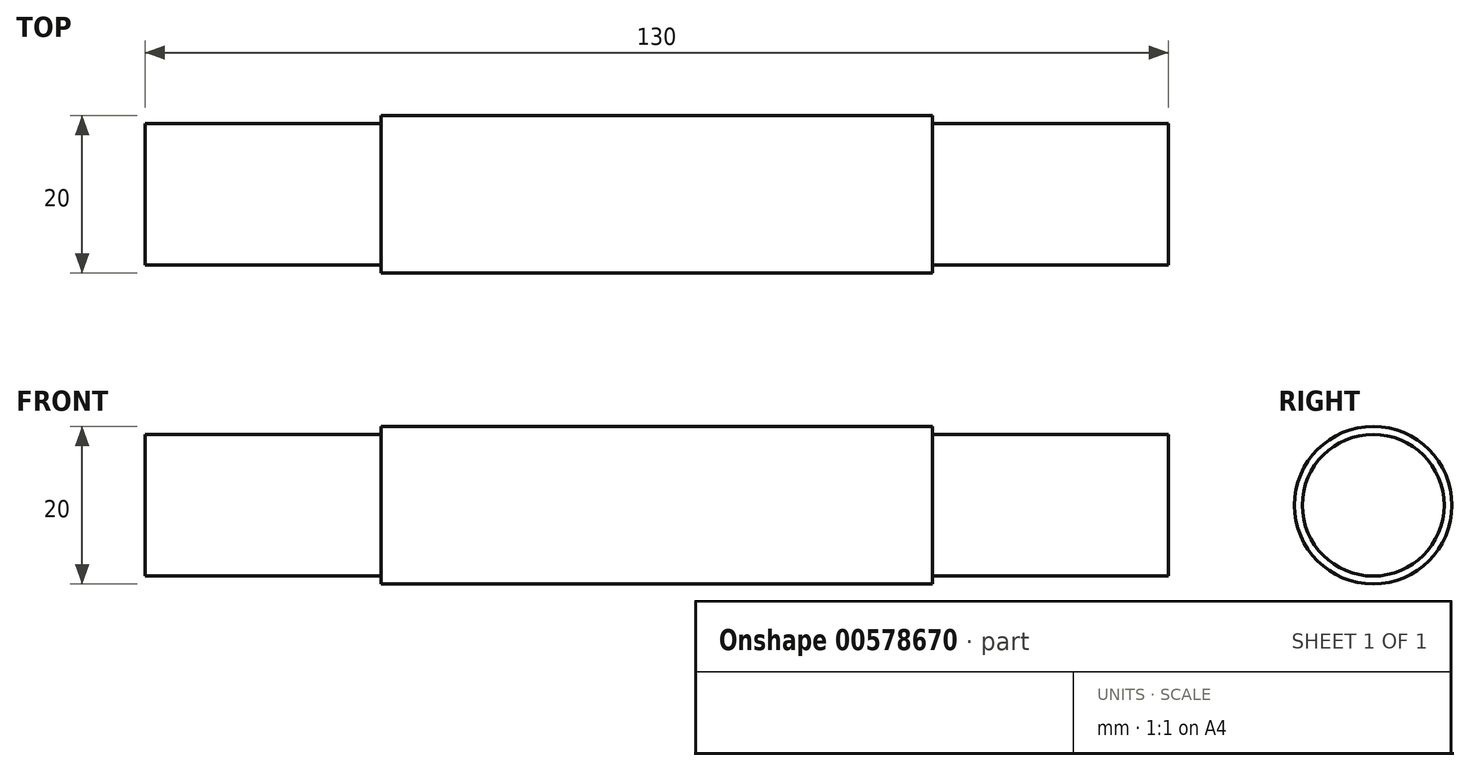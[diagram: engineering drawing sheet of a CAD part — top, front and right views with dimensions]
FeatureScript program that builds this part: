
annotation { "Feature Type Name" : "Feature", "Feature Type Description" : "" }
export const myFeature = defineFeature(function(context is Context, id is Id, definition is map)
    precondition{}
    {
        {
            var Q0;
            Q0=qCreatedBy(makeId("Top.planeOp"),FACE);
            var sketch = newSketch(context, id + "F0", { "sketchPlane" : qUnion([Q0])});
            skLineSegment(sketch, "E0", {"start": v(-42.44, 9) * mm, "end": v(-12.44, 9) * mm});
            skLineSegment(sketch, "E1", {"start": v(-12.44, 9) * mm, "end": v(-12.44, 10) * mm});
            skLineSegment(sketch, "E2", {"start": v(-12.44, 10) * mm, "end": v(57.56, 10) * mm});
            skLineSegment(sketch, "E3", {"start": v(57.56, 10) * mm, "end": v(57.56, 9) * mm});
            skLineSegment(sketch, "E4", {"start": v(57.56, 9) * mm, "end": v(87.56, 9) * mm});
            skLineSegment(sketch, "E5", {"start": v(87.56, 9) * mm, "end": v(87.56, 0) * mm});
            skLineSegment(sketch, "E6", {"start": v(-42.44, 9) * mm, "end": v(-42.44, 0) * mm});
            skLineSegment(sketch, "E7", {"start": v(-53.5, 0) * mm, "end": v(73.3, 0) * mm, "construction": true});
            skLineSegment(sketch, "E8", {"start": v(-42.44, 0) * mm, "end": v(87.56, 0) * mm});
            skLineSegment(sketch, "E9", {"start": v(22.56, 54.38) * mm, "end": v(22.56, -21.7) * mm, "construction": true});
            skSolve(sketch);
        }
        {
            var Q0;
            Q0=qSketchRegion(id+"F0",true);
            var Q1;
            Q1=sQuery(id+"F0.wireOp",EDGE,"E7");
            revolve(context, id + "F1", {"entities" : qUnion([Q0]), "axis" : qUnion([Q1]), "revolveType" : RevolveType.FULL});
        }
    });
